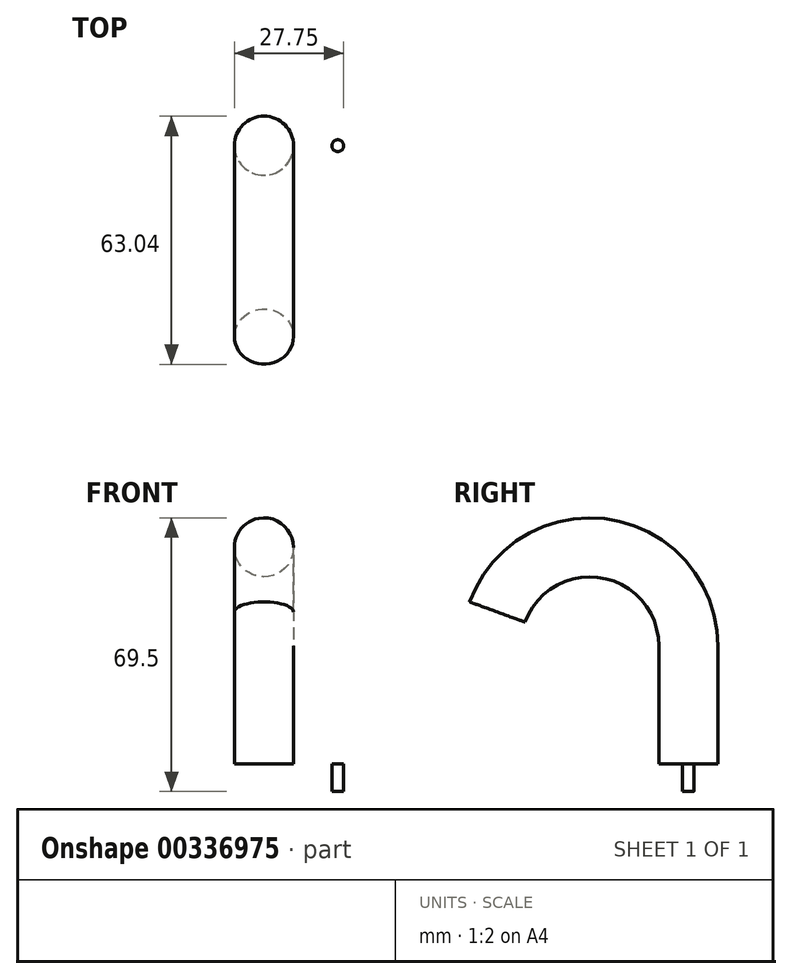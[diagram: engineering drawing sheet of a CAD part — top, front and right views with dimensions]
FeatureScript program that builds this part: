
annotation { "Feature Type Name" : "Feature", "Feature Type Description" : "" }
export const myFeature = defineFeature(function(context is Context, id is Id, definition is map)
    precondition{}
    {
        {
            var Q0;
            Q0=qCreatedBy(makeId("Top.planeOp"),FACE);
            var sketch = newSketch(context, id + "F0", { "sketchPlane" : qUnion([Q0])});
            skLineSegment(sketch, "E0.bottom", {"start": v(-50, 25) * mm, "end": v(50, 25) * mm});
            skLineSegment(sketch, "E0.top", {"start": v(-50, -25) * mm, "end": v(50, -25) * mm});
            skLineSegment(sketch, "E0.left", {"start": v(-50, 25) * mm, "end": v(-50, -25) * mm});
            skLineSegment(sketch, "E0.right", {"start": v(50, 25) * mm, "end": v(50, -25) * mm});
            skPoint(sketch, "E0.middle", {"position": v(0, 0) * mm});
            skPoint(sketch, "E1", {"position": v(36.17, 0) * mm});
            skPoint(sketch, "E2.MirrorP", {"position": v(-36.17, 0) * mm});
            skSolve(sketch);
        }
        {
            var Q0;
            Q0=makeQuery(id+"F0.imprint","IMPRINT",FACE,{"disambiguationData":[TD([[makeQuery(id+"F0.imprint","IMPRINT",EDGE,{"derivedFrom":sQuery(id+"F0.wireOp",EDGE,"E0.bottom")}),-1.0]])]});
            extrude(context, id + "F1", {"entities" : qUnion([Q0]), "depth" : 7 * mm});
        }
        {
            var Q0;
            Q0=makeQuery(id+"F1.opExtrude","CAP_FACE",FACE,{"disambiguationData":[OSD([sQuery(id+"F0.wireOp",EDGE,"E0.bottom"),sQuery(id+"F0.wireOp",EDGE,"E0.top"),sQuery(id+"F0.wireOp",EDGE,"E0.left"),sQuery(id+"F0.wireOp",EDGE,"E0.right")])],"isStart":false});
            var sketch = newSketch(context, id + "F2", { "sketchPlane" : qUnion([Q0])});
            skCircle(sketch, "E3", {"center": v(-18.75, 0) * mm, "radius": 1.5 * mm});
            skCircle(sketch, "E4.MirrorC", {"center": v(18.75, 0) * mm, "radius": 1.5 * mm});
            skSolve(sketch);
        }
        {
            var Q0;
            Q0=makeQuery(id+"F2.imprint","IMPRINT",FACE,{"disambiguationData":[TD([[makeQuery(id+"F2.imprint","IMPRINT",EDGE,{"derivedFrom":sQuery(id+"F2.wireOp",EDGE,"E4.MirrorC")}),-1.0]])]});
            var Q1;
            Q1=makeQuery(id+"F2.imprint","IMPRINT",FACE,{"disambiguationData":[TD([[makeQuery(id+"F2.imprint","IMPRINT",EDGE,{"derivedFrom":sQuery(id+"F2.wireOp",EDGE,"E3")}),1.0]])]});
            extrude(context, id + "F3", {"entities" : qUnion([Q0, Q1]), "operationType" : NewBodyOperationType.REMOVE, "oppositeDirection" : true, "depth" : 25 * mm});
        }
        {
            var Q0;
            Q0=makeQuery(id+"F1.opExtrude","CAP_FACE",FACE,{"disambiguationData":[OSD([sQuery(id+"F0.wireOp",EDGE,"E0.bottom"),sQuery(id+"F0.wireOp",EDGE,"E0.top"),sQuery(id+"F0.wireOp",EDGE,"E0.left"),sQuery(id+"F0.wireOp",EDGE,"E0.right")])],"isStart":false});
            var sketch = newSketch(context, id + "F4", { "sketchPlane" : qUnion([Q0])});
            skCircle(sketch, "E5", {"center": v(0, 0) * mm, "radius": 7.5 * mm});
            skLineSegment(sketch, "E6.bottom", {"start": v(0, -25) * mm, "end": v(5.07, -25) * mm});
            skLineSegment(sketch, "E6.top", {"start": v(0, -19.77) * mm, "end": v(5.07, -19.77) * mm});
            skLineSegment(sketch, "E6.left", {"start": v(0, -25) * mm, "end": v(0, -19.77) * mm});
            skLineSegment(sketch, "E6.right", {"start": v(5.07, -25) * mm, "end": v(5.07, -19.77) * mm});
            skSolve(sketch);
        }
        {
            var Q0;
            Q0=makeQuery(id+"F4.imprint","IMPRINT",FACE,{"disambiguationData":[TD([[makeQuery(id+"F4.imprint","IMPRINT",EDGE,{"derivedFrom":sQuery(id+"F4.wireOp",EDGE,"E5")}),1.0]])]});
            var Q1;
            Q1=makeQuery(id+"F4.imprint","IMPRINT",FACE,{"disambiguationData":[TD([[makeQuery(id+"F4.imprint","IMPRINT",EDGE,{"derivedFrom":sQuery(id+"F4.wireOp",EDGE,"E6.bottom")}),1.0]])]});
            extrude(context, id + "F5", {"entities" : qUnion([Q0, Q1]), "depth" : 30 * mm});
        }
        {
            var Q0;
            Q0=makeQuery(id+"F5.opExtrude","CAP_FACE",FACE,{"disambiguationData":[OSD([sQuery(id+"F4.wireOp",EDGE,"E5")])],"isStart":false});
            var sketch = newSketch(context, id + "F6", { "sketchPlane" : qUnion([Q0])});
            skCircle(sketch, "E7", {"center": v(0, 0) * mm, "radius": 7.5 * mm});
            skSolve(sketch);
        }
        {
            var Q0;
            Q0=makeQuery(id+"F6.imprint","IMPRINT",FACE,{"disambiguationData":[TD([[makeQuery(id+"F6.imprint","IMPRINT",EDGE,{"derivedFrom":sQuery(id+"F6.wireOp",EDGE,"E7")}),1.0]])]});
            var Q1;
            Q1=makeQuery(id+"F5.opExtrude","CAP_EDGE",EDGE,{"disambiguationData":[OSD([sQuery(id+"F4.wireOp",EDGE,"E6.bottom")])],"isStart":false});
            revolve(context, id + "F7", {"operationType" : NewBodyOperationType.ADD, "entities" : qUnion([Q0]), "axis" : qUnion([Q1]), "revolveType" : RevolveType.ONE_DIRECTION, "angle" : 160 * degree});
        }
        {
            var Q0;
            Q0=makeQuery(id+"F5.opExtrude","SWEPT_BODY",BODY,{"disambiguationData":[OSD([sQuery(id+"F4.wireOp",EDGE,"E6.bottom"),sQuery(id+"F4.wireOp",EDGE,"E6.top"),sQuery(id+"F4.wireOp",EDGE,"E6.left"),sQuery(id+"F4.wireOp",EDGE,"E6.right")])]});
            deleteBodies(context, id + "F8", {"entities" : qUnion([Q0])});
        }
    });
